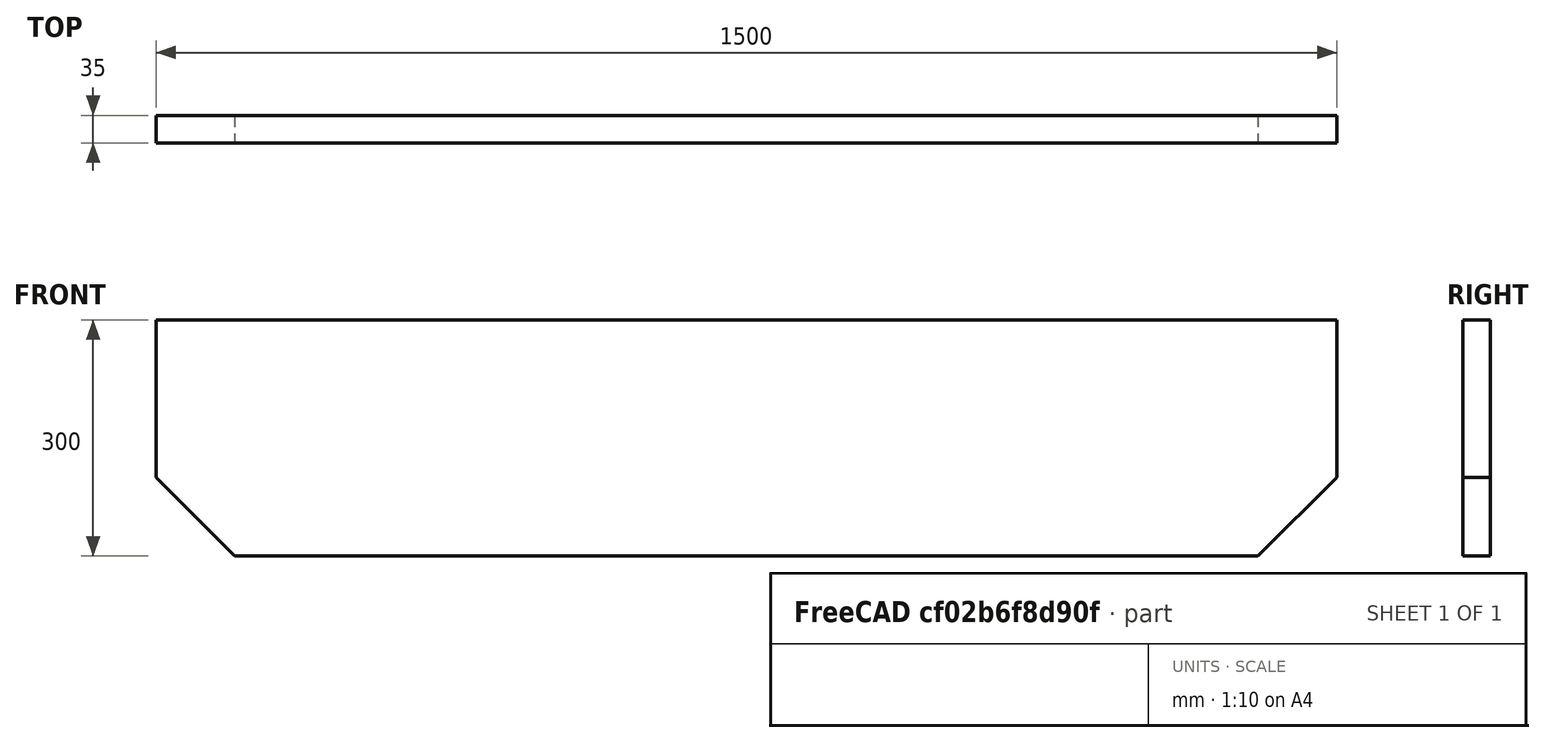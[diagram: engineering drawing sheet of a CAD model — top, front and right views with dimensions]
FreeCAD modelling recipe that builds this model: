
FCSTD DOCUMENT  (FreeCAD 0.18R4 (GitTag))
Label: apron_exterior
License: All rights reserved
LicenseURL: http://en.wikipedia.org/wiki/All_rights_reserved
objects: Sketcher::SketchObject×1, PartDesign::Pad×1, PartDesign::Body×1
note: 4 computed .brp shape members not serialized (recipe doc carries the construction recipe); baked Part::Feature solids carry a one-line shape summary decoded from their .brp

FEATURE [Sketcher::SketchObject] Sketch
  MapMode = 5
  Placement = pos=(0,0,0) rot=(1,0,0;1.5708rad)
  Support = -> [XZ_Plane]
  sketch-geometry (6):
    g0: LineSegment StartX=-100 StartY=0 StartZ=0 EndX=-1400 EndY=0 EndZ=0
    g1: LineSegment StartX=-100 StartY=0 StartZ=0 EndX=0 EndY=100 EndZ=0
    g2: LineSegment StartX=0 StartY=100 StartZ=0 EndX=0 EndY=300 EndZ=0
    g3: LineSegment StartX=0 StartY=300 StartZ=0 EndX=-1500 EndY=300 EndZ=0
    g4: LineSegment StartX=-1500 StartY=300 StartZ=0 EndX=-1500 EndY=100 EndZ=0
    g5: LineSegment StartX=-1500 StartY=100 StartZ=0 EndX=-1400 EndY=0 EndZ=0
  constraints (18):
    c: Coincident(g0,g1)
    c: Coincident(g1,g2)
    c: Coincident(g2,g3)
    c: Coincident(g4,g3)
    c: Coincident(g4,g5)
    c: Coincident(g5,g0)
    c: Vertical(g4)
    c: Vertical(g2)
    c: Horizontal(g3)
    c: Horizontal(g0)
    c: DistanceY(g0,g2) = 300
    c: DistanceX(g3,g3) = 1500
    c: PointOnObject(g1,g-2)
    c: PointOnObject(g0,g-1)
    c: Angle(g-1,g1) = 0.785398
    c: Angle(g-1,g5) = 2.35619
    c: DistanceY(g4,g4) = 200
    c: DistanceY(g2,g2) = 200
FEATURE [PartDesign::Pad] Pad
  Length = 35
  Length2 = 100
  Placement = pos=(0,0,0) rot=(1,0,0;1.5708rad)
  Profile = -> Sketch
  Type = 0
FEATURE [PartDesign::Body] Body
  Group = -> [Sketch,Pad]
  Origin = -> Origin
  Tip = -> Pad
